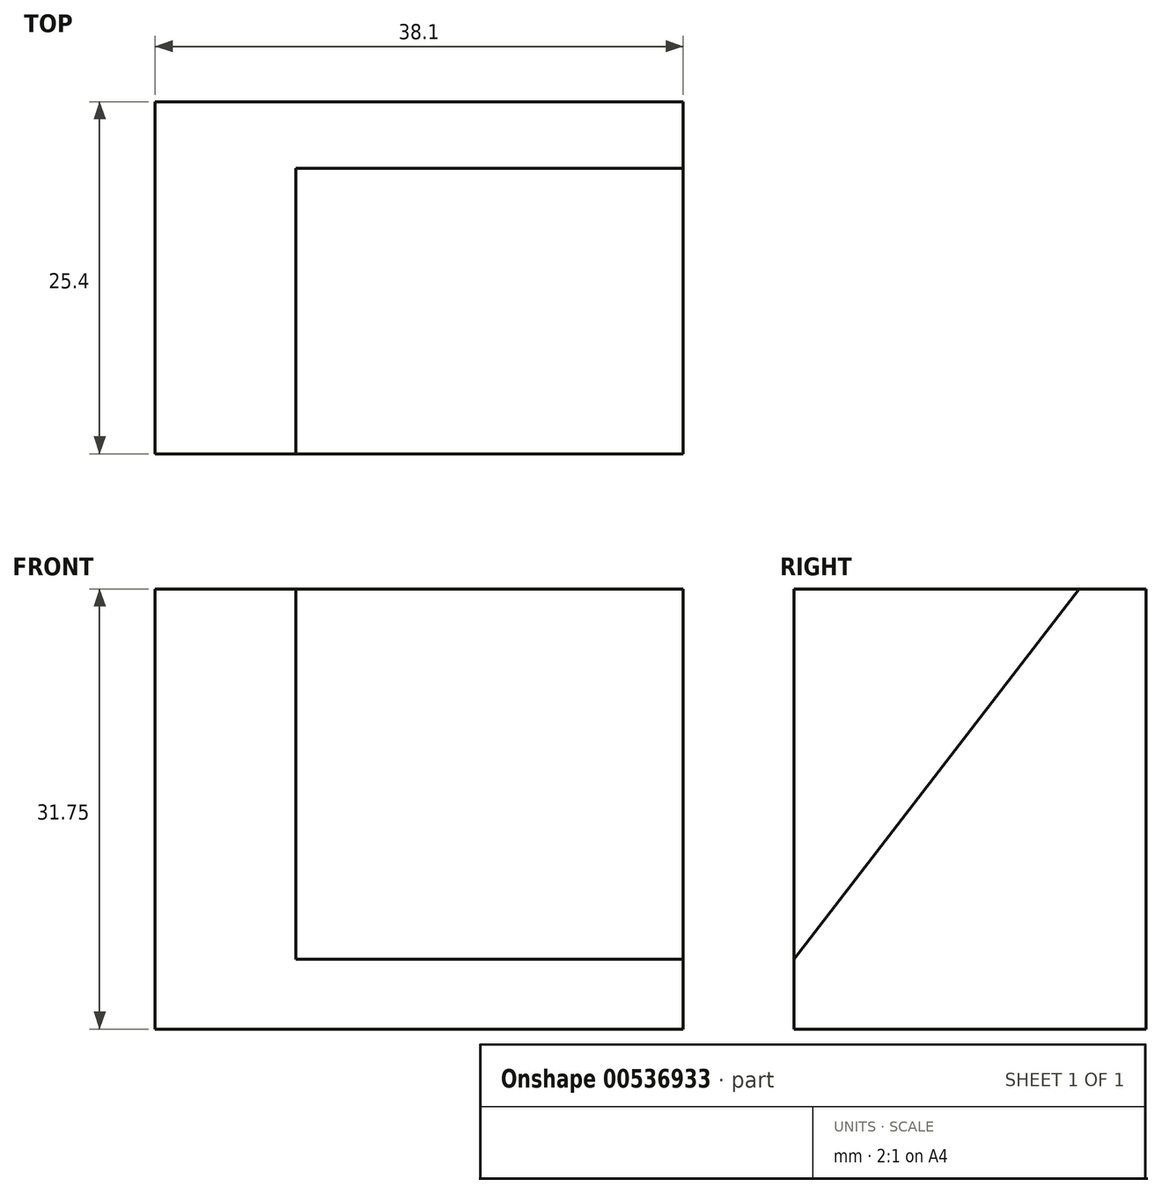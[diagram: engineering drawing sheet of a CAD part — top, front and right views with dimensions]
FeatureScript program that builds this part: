
annotation { "Feature Type Name" : "Feature", "Feature Type Description" : "" }
export const myFeature = defineFeature(function(context is Context, id is Id, definition is map)
    precondition{}
    {
        {
            var Q0;
            Q0=qCreatedBy(makeId("Front.planeOp"),FACE);
            var sketch = newSketch(context, id + "F0", { "sketchPlane" : qUnion([Q0])});
            skLineSegment(sketch, "E0.bottom", {"start": v(-41.08, 31.75) * mm, "end": v(-2.98, 31.75) * mm});
            skLineSegment(sketch, "E0.top", {"start": v(-41.08, 0) * mm, "end": v(-2.98, 0) * mm});
            skLineSegment(sketch, "E0.left", {"start": v(-41.08, 31.75) * mm, "end": v(-41.08, 0) * mm});
            skLineSegment(sketch, "E0.right", {"start": v(-2.98, 31.75) * mm, "end": v(-2.98, 0) * mm});
            skSolve(sketch);
        }
        {
            var Q0;
            Q0=makeQuery(id+"F0.imprint","IMPRINT",FACE,{"disambiguationData":[TD([[makeQuery(id+"F0.imprint","IMPRINT",EDGE,{"derivedFrom":sQuery(id+"F0.wireOp",EDGE,"E0.bottom")}),-1.0]])]});
            extrude(context, id + "F1", {"entities" : qUnion([Q0]), "depth" : 25.4 * mm, "offsetDistance" : 25.4 * mm});
        }
        {
            var Q0;
            Q0=makeQuery(id+"F1.opExtrude","SWEPT_FACE",FACE,{"disambiguationData":[OSD([sQuery(id+"F0.wireOp",EDGE,"E0.right")])]});
            var sketch = newSketch(context, id + "F2", { "sketchPlane" : qUnion([Q0])});
            skLineSegment(sketch, "E1", {"start": v(-4.82, 31.75) * mm, "end": v(-25.4, 5.03) * mm});
            skLineSegment(sketch, "E2", {"start": v(-25.4, 5.03) * mm, "end": v(0, 5.03) * mm});
            skLineSegment(sketch, "E3", {"start": v(0, 5.03) * mm, "end": v(0, 31.75) * mm});
            skLineSegment(sketch, "E4", {"start": v(0, 31.75) * mm, "end": v(-4.82, 31.75) * mm});
            skSolve(sketch);
        }
        {
            var Q0;
            {var subQ0=sQuery(id+"F2.wireOp",EDGE,"E1");Q0=makeQuery(id+"F2.imprint","IMPRINT",FACE,{"disambiguationData":[TD([[makeQuery(id+"F2.imprint","IMPRINT",EDGE,{"derivedFrom":subQ0}),-1.0]])]});}
            extrude(context, id + "F3", {"entities" : qUnion([Q0]), "operationType" : NewBodyOperationType.REMOVE, "oppositeDirection" : true, "depth" : 27.94 * mm, "offsetDistance" : 25.4 * mm});
        }
    });
